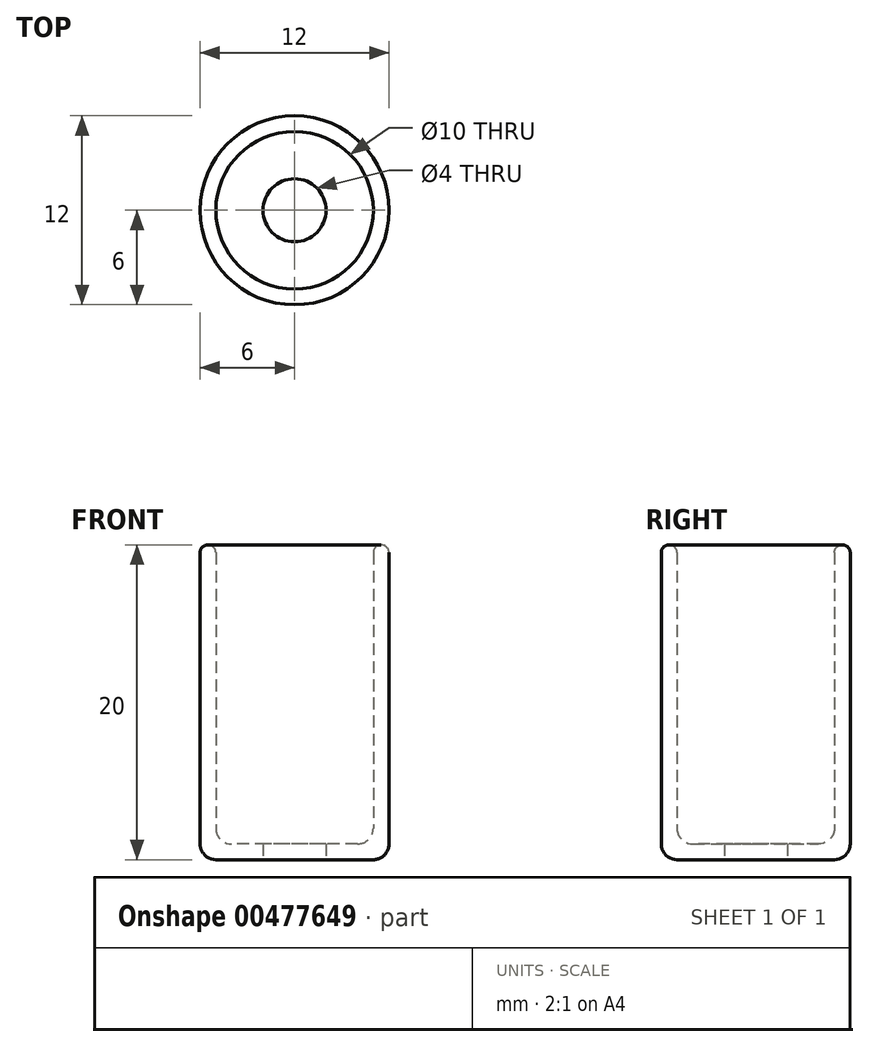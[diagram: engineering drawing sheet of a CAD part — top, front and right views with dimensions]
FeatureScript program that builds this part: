
annotation { "Feature Type Name" : "Feature", "Feature Type Description" : "" }
export const myFeature = defineFeature(function(context is Context, id is Id, definition is map)
    precondition{}
    {
        {
            var Q0;
            Q0=qCreatedBy(makeId("Top.planeOp"),FACE);
            var sketch = newSketch(context, id + "F0", { "sketchPlane" : qUnion([Q0])});
            skCircle(sketch, "E0", {"center": v(0, 0) * mm, "radius": 6 * mm});
            skCircle(sketch, "E1", {"center": v(0, 0) * mm, "radius": 2 * mm});
            skSolve(sketch);
        }
        {
            var Q0;
            Q0=makeQuery(id+"F0.imprint","IMPRINT",FACE,{"disambiguationData":[TD([[makeQuery(id+"F0.imprint","IMPRINT",EDGE,{"derivedFrom":sQuery(id+"F0.wireOp",EDGE,"E0")}),1.0]])]});
            var Q1;
            Q1=makeQuery(id+"F0.imprint","IMPRINT",FACE,{"disambiguationData":[TD([[makeQuery(id+"F0.imprint","IMPRINT",EDGE,{"derivedFrom":sQuery(id+"F0.wireOp",EDGE,"E1")}),1.0]])]});
            extrude(context, id + "F1", {"entities" : qUnion([Q0, Q1]), "depth" : 20 * mm});
        }
        {
            var Q0;
            Q0=makeQuery(id+"F1.opExtrude","CAP_FACE",FACE,{"disambiguationData":[OSD([sQuery(id+"F0.wireOp",EDGE,"E0")])],"isStart":false});
            shell(context, id + "F2", {"entities" : qUnion([Q0]), "thickness" : 1 * mm});
        }
        {
            var Q0;
            Q0=makeQuery(id+"F0.imprint","IMPRINT",FACE,{"disambiguationData":[TD([[makeQuery(id+"F0.imprint","IMPRINT",EDGE,{"derivedFrom":sQuery(id+"F0.wireOp",EDGE,"E1")}),1.0]])]});
            extrude(context, id + "F3", {"entities" : qUnion([Q0]), "operationType" : NewBodyOperationType.REMOVE, "depth" : 25 * mm});
        }
        {
            var Q0;
            Q0=makeQuery(id+"F1.opExtrude","CAP_EDGE",EDGE,{"disambiguationData":[OSD([sQuery(id+"F0.wireOp",EDGE,"E0")])],"isStart":true});
            var Q1;
            {var subQ0=sQuery(id+"F0.wireOp",EDGE,"E0");Q1=makeQuery(id+"F2.opShell","OFFSET_EDGE",EDGE,{"disambiguationData":[OSD([subQ0]),TDD([makeQuery(id+"F1.opExtrude","CAP_EDGE",EDGE,{"disambiguationData":[OSD([subQ0])],"isStart":true})])]});}
            fillet(context, id + "F4", {"entities" : qUnion([Q0, Q1]), "radius" : 1 * mm, "tangentPropagation" : true, "allowEdgeOverflow" : false});
        }
        {
            var Q0;
            {var subQ0=sQuery(id+"F0.wireOp",EDGE,"E0");Q0=makeQuery(id+"Fn7VKt0e6IIinrH_1.opChamfer","BLEND_EDGE",EDGE,{"blendedFrom":[makeQuery(id+"F2.opShell","OFFSET_EDGE",EDGE,{"disambiguationData":[OSD([subQ0]),TDD([makeQuery(id+"F1.opExtrude","CAP_EDGE",EDGE,{"disambiguationData":[OSD([subQ0])],"isStart":false})])]}),makeQuery(id+"F2.opShell","OFFSET_FACE",FACE,{"disambiguationData":[OSD([subQ0]),TDD([makeQuery(id+"F1.opExtrude","SWEPT_FACE",FACE,{"disambiguationData":[OSD([subQ0])]})])]})],"blendedInto":[makeQuery(id+"F2.opShell","OFFSET_FACE",FACE,{"disambiguationData":[OSD([subQ0]),TDD([makeQuery(id+"F1.opExtrude","SWEPT_FACE",FACE,{"disambiguationData":[OSD([subQ0])]})])]})]});}
            var Q1;
            {var subQ0=sQuery(id+"F0.wireOp",EDGE,"E0");Q1=makeQuery(id+"F2.opShell","OFFSET_EDGE",EDGE,{"disambiguationData":[OSD([subQ0]),TDD([makeQuery(id+"F1.opExtrude","CAP_EDGE",EDGE,{"disambiguationData":[OSD([subQ0])],"isStart":false})])]});}
            var Q2;
            Q2=makeQuery(id+"F1.opExtrude","CAP_EDGE",EDGE,{"disambiguationData":[OSD([sQuery(id+"F0.wireOp",EDGE,"E0")])],"isStart":false});
            fillet(context, id + "F5", {"entities" : qUnion([Q0, Q1, Q2]), "radius" : .5 * mm, "tangentPropagation" : true, "allowEdgeOverflow" : false});
        }
    });
